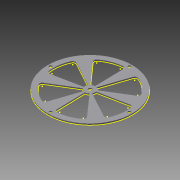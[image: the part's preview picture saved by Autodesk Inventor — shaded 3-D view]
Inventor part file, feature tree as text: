
AUTODESK INVENTOR PART (.ipt)
format: ipt  version: 2013 (Build 170138000, 138)  size: 207,872 bytes
history: native  units: in
note: dims shown in document units (in); Inventor stores cm internally (conversion verified against a paired STEP export)
features: extrude x3, sketch x3, fillet x1
ambient origin geometry x8: Origin, YZ Plane, XZ Plane, XY Plane, X Axis, Y Axis, Z Axis, Center Point
bodies: Solid1 (feature_tree)
feature tree (7):
  extrude  "Extrusion1"  Depth=7.0in
  fillet  "Fillet1"  Radius=0.266in
  extrude  "Extrusion2"  Depth=0.266in
  extrude  "Extrusion3"  Depth=7.5in
  sketch  "Sketch1"  dims[d0=8.0in d1=7.0in d2=0.266in]
  sketch  "Sketch2"  dims[d3=0.266in d4=0.266in]
  sketch  "Sketch3"  dims[d5=0.266in d6=7.5in d7=3.75in d8=3.75in d9=3.75in d10=3.75in d12=1.0in d13=0.375in d14=0.0in d15=0.0in d16=0.1374in d17=2.3622in d19=360.0deg d21=0.125in d22=0.0in d23=0.25in d24=0.315in d25=0.125in d26=0.0in d27=0.0787in d29=0.0394in d30=0.0394in d31=0.25in d32=0.0in]
